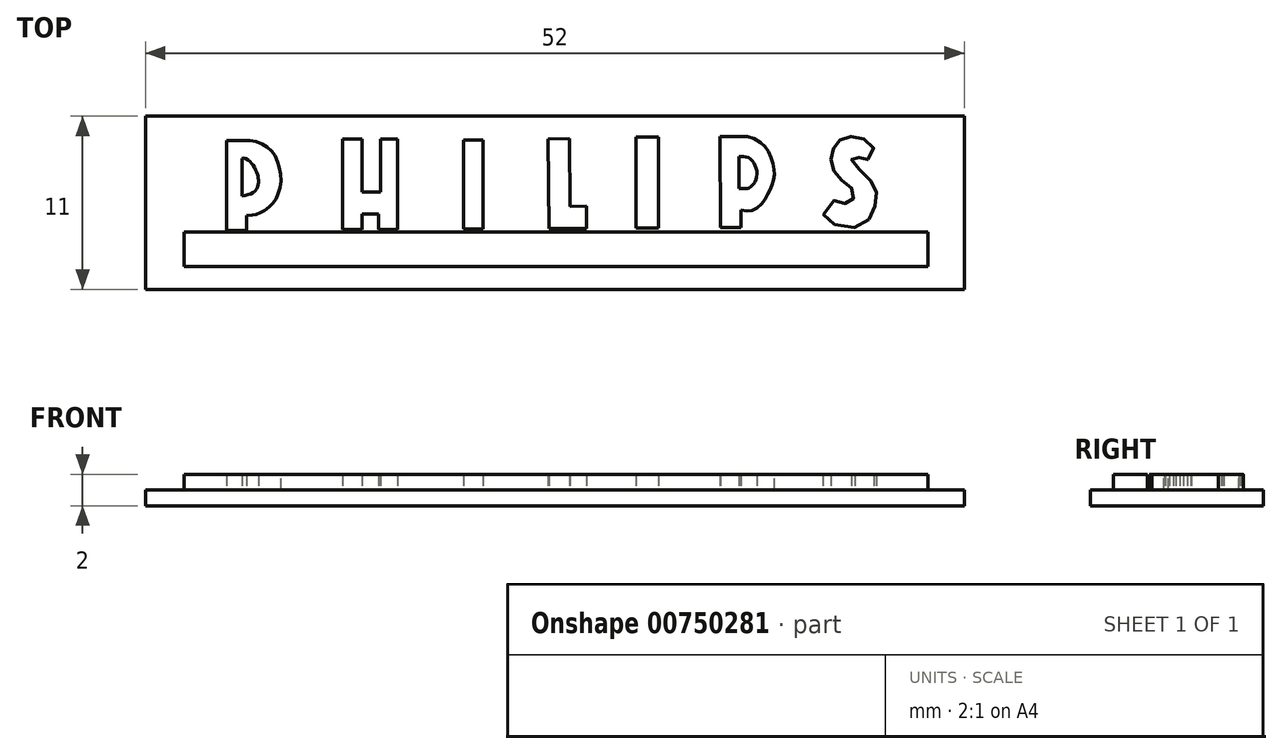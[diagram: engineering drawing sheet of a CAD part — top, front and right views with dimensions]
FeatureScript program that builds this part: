
annotation { "Feature Type Name" : "Feature", "Feature Type Description" : "" }
export const myFeature = defineFeature(function(context is Context, id is Id, definition is map)
    precondition{}
    {
        {
            var Q0;
            Q0=qCreatedBy(makeId("Top.planeOp"),FACE);
            var sketch = newSketch(context, id + "F0", { "sketchPlane" : qUnion([Q0])});
            skLineSegment(sketch, "E0.bottom", {"start": v(-13.83, 9.02) * mm, "end": v(38.17, 9.02) * mm});
            skLineSegment(sketch, "E0.top", {"start": v(-13.83, -1.98) * mm, "end": v(38.17, -1.98) * mm});
            skLineSegment(sketch, "E0.left", {"start": v(-13.83, 9.02) * mm, "end": v(-13.83, -1.98) * mm});
            skLineSegment(sketch, "E0.right", {"start": v(38.17, 9.02) * mm, "end": v(38.17, -1.98) * mm});
            skSolve(sketch);
        }
        {
            var Q0;
            Q0 = qSketchRegion(id + "F0", true);
            extrude(context, id + "F1", {"entities" : qUnion([Q0]), "depth" : 1 * mm, "offsetDistance" : 25 * mm});
        }
        {
            var Q0;
            Q0=makeQuery(id+"F1.opExtrude","CAP_FACE",FACE,{"disambiguationData":[OSD([sQuery(id+"F0.wireOp",EDGE,"E0.bottom"),sQuery(id+"F0.wireOp",EDGE,"E0.top"),sQuery(id+"F0.wireOp",EDGE,"E0.left"),sQuery(id+"F0.wireOp",EDGE,"E0.right")])],"isStart":false});
            var sketch = newSketch(context, id + "F2", { "sketchPlane" : qUnion([Q0])});
            skLineSegment(sketch, "E1", {"start": v(-7.71, 6.33) * mm, "end": v(-7.71, 3.94) * mm});
            skFitSpline(sketch, "E2", {"points": [v(-7.71, 6.33) * mm, v(-7.5, 6.33) * mm, v(-7.15, 6.09) * mm, v(-6.95, 5.82) * mm, v(-6.77, 5.43) * mm, v(-6.7, 5.18) * mm, v(-6.66, 4.93) * mm, v(-6.68, 4.64) * mm, v(-6.84, 4.32) * mm, v(-7.16, 4.08) * mm, v(-7.71, 3.94) * mm], "startDerivative": vector(2.8, 0.6) * mm, "endDerivative": vector(-4.5, -0.9) * mm});
            skLineSegment(sketch, "E3", {"start": v(-8.68, 1.77) * mm, "end": v(-7.4, 1.77) * mm});
            skLineSegment(sketch, "E4", {"start": v(-7.4, 1.77) * mm, "end": v(-7.4, 2.71) * mm});
            skLineSegment(sketch, "E5", {"start": v(-8.68, 1.77) * mm, "end": v(-8.68, 7.46) * mm});
            skFitSpline(sketch, "E6", {"points": [v(-8.68, 7.46) * mm, v(-8.33, 7.46) * mm, v(-7.93, 7.46) * mm, v(-7.51, 7.46) * mm, v(-7.21, 7.46) * mm, v(-6.85, 7.4) * mm, v(-6.41, 7.26) * mm, v(-6.1, 7.07) * mm, v(-5.84, 6.82) * mm, v(-5.63, 6.52) * mm, v(-5.44, 6.08) * mm, v(-5.34, 5.76) * mm, v(-5.24, 5.25) * mm, v(-5.25, 4.74) * mm, v(-5.32, 4.35) * mm, v(-5.5, 3.92) * mm, v(-5.63, 3.63) * mm, v(-5.85, 3.35) * mm, v(-6, 3.22) * mm, v(-6.29, 3.02) * mm, v(-6.49, 2.9) * mm, v(-6.76, 2.77) * mm, v(-6.91, 2.76) * mm, v(-7.09, 2.72) * mm, v(-7.4, 2.71) * mm], "startDerivative": vector(8.13, 0) * mm, "endDerivative": vector(-8.52, 0.3) * mm});
            skLineSegment(sketch, "E7", {"start": v(-1.31, 1.81) * mm, "end": v(-0.08, 1.81) * mm});
            skLineSegment(sketch, "E8", {"start": v(-0.08, 1.81) * mm, "end": v(-0.08, 2.8) * mm});
            skLineSegment(sketch, "E9", {"start": v(-0.08, 2.8) * mm, "end": v(0.96, 2.8) * mm});
            skLineSegment(sketch, "E10", {"start": v(0.96, 2.8) * mm, "end": v(0.96, 1.81) * mm});
            skLineSegment(sketch, "E11", {"start": v(0.96, 1.81) * mm, "end": v(2.18, 1.81) * mm});
            skLineSegment(sketch, "E12", {"start": v(2.18, 7.57) * mm, "end": v(2.18, 1.81) * mm});
            skLineSegment(sketch, "E13", {"start": v(2.18, 7.57) * mm, "end": v(1.1, 7.57) * mm});
            skLineSegment(sketch, "E14", {"start": v(1.1, 7.57) * mm, "end": v(1.1, 4.2) * mm});
            skLineSegment(sketch, "E15", {"start": v(1.1, 4.2) * mm, "end": v(-0.08, 4.2) * mm});
            skLineSegment(sketch, "E16", {"start": v(-0.08, 4.2) * mm, "end": v(-0.08, 7.57) * mm});
            skLineSegment(sketch, "E17", {"start": v(-0.08, 7.57) * mm, "end": v(-1.31, 7.57) * mm});
            skLineSegment(sketch, "E18", {"start": v(-1.31, 7.57) * mm, "end": v(-1.31, 1.81) * mm});
            skLineSegment(sketch, "E19.bottom", {"start": v(6.35, 1.86) * mm, "end": v(7.58, 1.86) * mm});
            skLineSegment(sketch, "E19.top", {"start": v(6.35, 7.49) * mm, "end": v(7.58, 7.49) * mm});
            skLineSegment(sketch, "E19.left", {"start": v(6.35, 1.86) * mm, "end": v(6.35, 7.49) * mm});
            skLineSegment(sketch, "E19.right", {"start": v(7.58, 1.86) * mm, "end": v(7.58, 7.49) * mm});
            skLineSegment(sketch, "E20", {"start": v(-11.44, 1.74) * mm, "end": v(30.51, 1.98) * mm});
            skLineSegment(sketch, "E21", {"start": v(12.23, 1.87) * mm, "end": v(14.42, 1.89) * mm});
            skLineSegment(sketch, "E22", {"start": v(11.8, 1.87) * mm, "end": v(14.17, 1.88) * mm});
            skLineSegment(sketch, "E23", {"start": v(14.17, 1.88) * mm, "end": v(14.17, 3.3) * mm});
            skLineSegment(sketch, "E24", {"start": v(14.17, 3.3) * mm, "end": v(13.13, 3.3) * mm});
            skLineSegment(sketch, "E25", {"start": v(13.13, 3.3) * mm, "end": v(13.1, 7.58) * mm});
            skLineSegment(sketch, "E26", {"start": v(13.1, 7.58) * mm, "end": v(11.71, 7.58) * mm});
            skLineSegment(sketch, "E27", {"start": v(11.71, 7.58) * mm, "end": v(11.8, 1.87) * mm});
            skLineSegment(sketch, "E28.bottom", {"start": v(17.32, 7.68) * mm, "end": v(18.74, 7.68) * mm});
            skLineSegment(sketch, "E28.top", {"start": v(17.32, 1.91) * mm, "end": v(18.74, 1.91) * mm});
            skLineSegment(sketch, "E28.left", {"start": v(17.32, 7.68) * mm, "end": v(17.32, 1.91) * mm});
            skLineSegment(sketch, "E28.right", {"start": v(18.74, 7.68) * mm, "end": v(18.74, 1.91) * mm});
            skLineSegment(sketch, "E29", {"start": v(22.65, 7.72) * mm, "end": v(22.69, 1.93) * mm});
            skLineSegment(sketch, "E30", {"start": v(23.84, 6.44) * mm, "end": v(23.85, 4.42) * mm});
            skLineSegment(sketch, "E31", {"start": v(23.99, 3.05) * mm, "end": v(24, 1.94) * mm});
            skFitSpline(sketch, "E32", {"points": [v(23.84, 6.44) * mm, v(24.23, 6.44) * mm, v(24.61, 6.27) * mm, v(24.88, 5.88) * mm, v(25, 5.32) * mm, v(24.85, 4.8) * mm, v(24.7, 4.63) * mm, v(24.43, 4.42) * mm, v(24.2, 4.42) * mm, v(23.85, 4.42) * mm], "startDerivative": vector(3.63, 0.6) * mm, "endDerivative": vector(-3.38, -0.14) * mm});
            skFitSpline(sketch, "E33", {"points": [v(22.65, 7.72) * mm, v(23.25, 7.72) * mm, v(23.7, 7.72) * mm, v(23.98, 7.72) * mm, v(24.46, 7.72) * mm, v(25.15, 7.4) * mm, v(25.6, 6.98) * mm, v(25.86, 6.47) * mm, v(26.04, 5.88) * mm, v(26.1, 5.44) * mm, v(26.06, 5.02) * mm, v(25.92, 4.57) * mm, v(25.77, 4.22) * mm, v(25.56, 3.83) * mm, v(25.26, 3.44) * mm, v(24.88, 3.11) * mm, v(24.5, 3) * mm, v(23.99, 3.05) * mm], "startDerivative": vector(9.35, -0.02) * mm, "endDerivative": vector(-8.72, 1.67) * mm});
            skLineSegment(sketch, "E34.trimOffspring", {"start": v(31.68, 1.98) * mm, "end": v(35.9, 2) * mm});
            skFitSpline(sketch, "E35", {"points": [v(30.27, 7.5) * mm, v(30.04, 7.3) * mm, v(29.9, 7.03) * mm, v(29.77, 6.7) * mm, v(29.7, 6.37) * mm, v(29.72, 5.98) * mm, v(29.84, 5.6) * mm, v(30.1, 5.26) * mm, v(30.4, 4.94) * mm, v(30.7, 4.69) * mm, v(31.02, 4.44) * mm, v(31.21, 4.14) * mm, v(31.14, 3.79) * mm, v(30.97, 3.56) * mm, v(30.64, 3.46) * mm, v(30.32, 3.55) * mm, v(29.98, 3.7) * mm, v(29.2, 2.95) * mm, v(29.35, 2.62) * mm, v(29.8, 2.22) * mm, v(30.88, 1.94) * mm, v(31.7, 2.1) * mm, v(32.21, 2.6) * mm, v(32.45, 3.14) * mm, v(32.56, 3.64) * mm, v(32.57, 4.13) * mm, v(32.44, 4.6) * mm, v(32.18, 4.97) * mm, v(31.68, 5.5) * mm, v(31.15, 5.9) * mm, v(31, 6.23) * mm, v(31.12, 6.46) * mm, v(31.34, 6.48) * mm, v(31.63, 6.28) * mm, v(31.76, 6.16) * mm, v(32.16, 6.33) * mm, v(32.44, 6.8) * mm, v(32.26, 7.23) * mm, v(31.89, 7.5) * mm, v(31.54, 7.66) * mm, v(30.98, 7.74) * mm, v(30.56, 7.64) * mm, v(30.27, 7.5) * mm]});
            skLineSegment(sketch, "E36.bottom", {"start": v(-11.37, -0.53) * mm, "end": v(35.87, -0.53) * mm});
            skLineSegment(sketch, "E36.top", {"start": v(-11.37, 1.65) * mm, "end": v(35.87, 1.65) * mm});
            skLineSegment(sketch, "E36.left", {"start": v(-11.37, -0.53) * mm, "end": v(-11.37, 1.65) * mm});
            skLineSegment(sketch, "E36.right", {"start": v(35.87, -0.53) * mm, "end": v(35.87, 1.65) * mm});
            skSolve(sketch);
        }
        {
            var Q0;
            Q0 = qSketchRegion(id + "F2", true);
            extrude(context, id + "F3", {"entities" : qUnion([Q0]), "operationType" : NewBodyOperationType.ADD, "depth" : 1 * mm, "offsetDistance" : 25 * mm});
        }
    });
